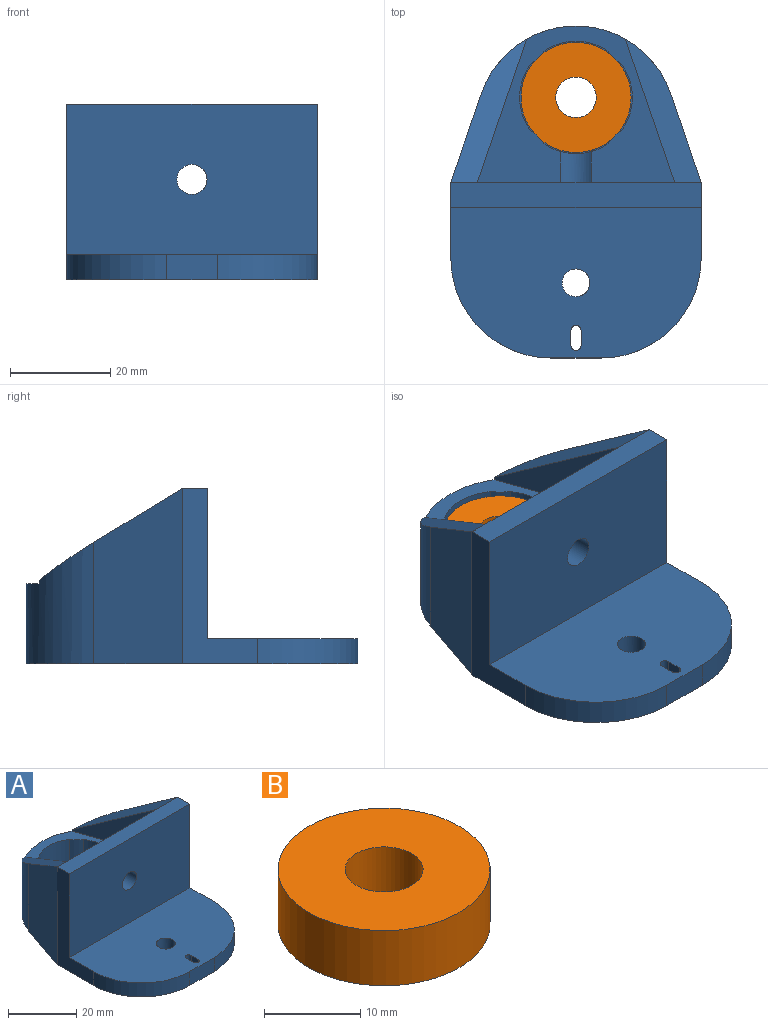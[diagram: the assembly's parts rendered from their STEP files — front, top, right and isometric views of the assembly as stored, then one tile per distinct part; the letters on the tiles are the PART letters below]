
ASSEMBLY  parts=2 mates=1
PART A: 36 faces, bbox 50x66.3x35 mm
  f0: cylinder r=11.25mm len=12.78mm, axis (0,0,-1), area 108.7mm2, adj f5,f9,f34,f35
  f1: cylinder r=11.25mm len=12.78mm, axis (0,0,-1), area 104.6mm2, adj f5,f9,f25,f32,f34
  f2: cylinder r=11.25mm len=12.78mm, axis (0,0,-1), area 108.7mm2, adj f5,f9,f33,f35
  f3: plane 66.25x50mm, normal (0,0,-1), area 2618mm2, adj f10,f11,f13,f14,f15,f20,f21,f22
  f4: plane 50x30mm, normal (0,0,1), area 1295mm2, adj f7,f11,f13,f22,f23,f26,f27,f28
  f5: plane 39.43x31.25mm, normal (0,0,1), area 452.6mm2, adj f0,f1,f2,f6,f8,f17,f19,f20
  f6: cylinder r=11.25mm len=12.78mm, axis (0,0,-1), area 108.7mm2, adj f5,f9,f32,f33
  f7: plane 50x30mm, normal (0,-1,0), area 1471.7mm2, adj f4,f11,f12,f13,f24
  f8: plane 50x20mm, normal (0,1,0), area 730.1mm2, adj f5,f12,f16,f17,f18,f19,f24,f25
  f9: plane 22.5x22.5mm, normal (0,0,1), area 315.3mm2, adj f0,f1,f2,f6,f10,f32,f33,f34
  f10: cylinder r=5mm len=10mm, axis (0,0,-1), area 251.3mm2, adj f3,f9
  f11: plane 35x15mm, normal (1,0,0), area 225mm2, adj f3,f4,f7,f12,f15,f31
  f12: plane 50x5mm, normal (0,0,1), area 250mm2, adj f7,f8,f11,f13
  f13: plane 35x15mm, normal (-1,0,0), area 225mm2, adj f3,f4,f7,f12,f14,f30
  f14: plane 35x17.76mm, normal (-0.95,0.33,0), area 555.8mm2, adj f3,f13,f16,f21
  f15: plane 35x17.76mm, normal (0.95,0.33,0), area 555.8mm2, adj f3,f11,f18,f20
  f16: plane 28.64x18.4mm, normal (0.16,0.47,0.87), area 155.6mm2, adj f8,f14,f17,f21
  f17: plane 28.64x18.01mm, normal (0.95,-0.33,0), area 281.8mm2, adj f5,f8,f16,f21
  f18: plane 28.64x18.4mm, normal (-0.16,0.47,0.87), area 155.6mm2, adj f8,f15,f19,f20
  f19: plane 28.64x18.01mm, normal (-0.95,-0.33,0), area 281.8mm2, adj f5,f8,f18,f20
  f20: cylinder r=20mm len=24.2mm, axis (0,0,1), area 457.4mm2, adj f3,f5,f15,f18,f19,f21
  f21: cylinder r=20mm len=24.2mm, axis (0,0,-1), area 457.4mm2, adj f3,f5,f14,f16,f17,f20
  f22: plane 10x5mm, normal (0,-1,0), area 50mm2, adj f3,f4,f30,f31
  f23: cylinder r=2.77mm len=5.55mm, axis (0,0,-1), area 87.2mm2, adj f3,f4
  f24: cylinder r=3mm len=6mm, axis (0,1,0), area 94.2mm2, adj f7,f8
  f25: cylinder r=5mm len=6.16mm, axis (0,1,0), area 37.9mm2, adj f1,f5,f8
  f26: plane 5x3mm, normal (-1,0,0), area 15mm2, adj f3,f4,f28,f29
  f27: plane 5x3mm, normal (1,0,0), area 15mm2, adj f3,f4,f28,f29
  f28: cylinder r=1mm len=5mm, axis (0,0,1), area 15.7mm2, adj f3,f4,f26,f27
  f29: cylinder r=1mm len=5mm, axis (0,0,-1), area 15.7mm2, adj f3,f4,f26,f27
  f30: cylinder r=20mm len=20mm, axis (0,0,-1), area 157.1mm2, adj f3,f4,f13,f22
  f31: cylinder r=20mm len=20mm, axis (0,0,1), area 157.1mm2, adj f3,f4,f11,f22
  f32: cylinder r=12.5mm len=8mm, axis (0,0,1), area 32.6mm2, adj f1,f5,f6,f9
  f33: cylinder r=12.5mm len=8mm, axis (0,0,1), area 32.6mm2, adj f2,f5,f6,f9
  f34: cylinder r=12.5mm len=8mm, axis (0,0,1), area 32.6mm2, adj f0,f1,f5,f9
  f35: cylinder r=12.5mm len=8mm, axis (0,0,1), area 32.6mm2, adj f0,f2,f5,f9
PART B: 4 faces, bbox 22x22x7 mm
  f0: cylinder r=4.05mm len=8.1mm, axis (0,0,-1), area 178.1mm2, adj f2,f3
  f1: cylinder r=11mm len=22mm, axis (0,0,-1), area 483.8mm2, adj f2,f3
  f2: plane 22x22mm, normal (0,0,1), area 328.6mm2, adj f0,f1
  f3: plane 22x22mm, normal (0,0,-1), area 328.6mm2, adj f0,f1
PLACE A t=(-7.15,17.8,-4.92)mm
PLACE B rot(axis=(1,0,0),180deg) t=(-7.15,17.8,2.08)mm
MATE fastened B.f0 <-> A.f10  axis (0,0,-1) through (-7.15,17.8,-4.92)mm
